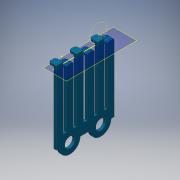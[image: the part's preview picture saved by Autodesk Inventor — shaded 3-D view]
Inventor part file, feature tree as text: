
AUTODESK INVENTOR PART (.ipt)
format: ipt  version: 2016 (Build 200138000, 138)  size: 192,512 bytes
history: native  units: in
note: dims shown in document units (in); Inventor stores cm internally (conversion verified against a paired STEP export)
features: other x3, sketch x1
ambient origin geometry x8: Origin, YZ Plane, XZ Plane, XY Plane, X Axis, Y Axis, Z Axis, Center Point
bodies: Solid1 (feature_tree)
feature tree (4):
  other  "Level1.ipt"
  other  "Solid1::Level1.ipt"
  other  "TaggingFeature1"
  sketch  "Sketch6"  dims[d0=0.4331in]
